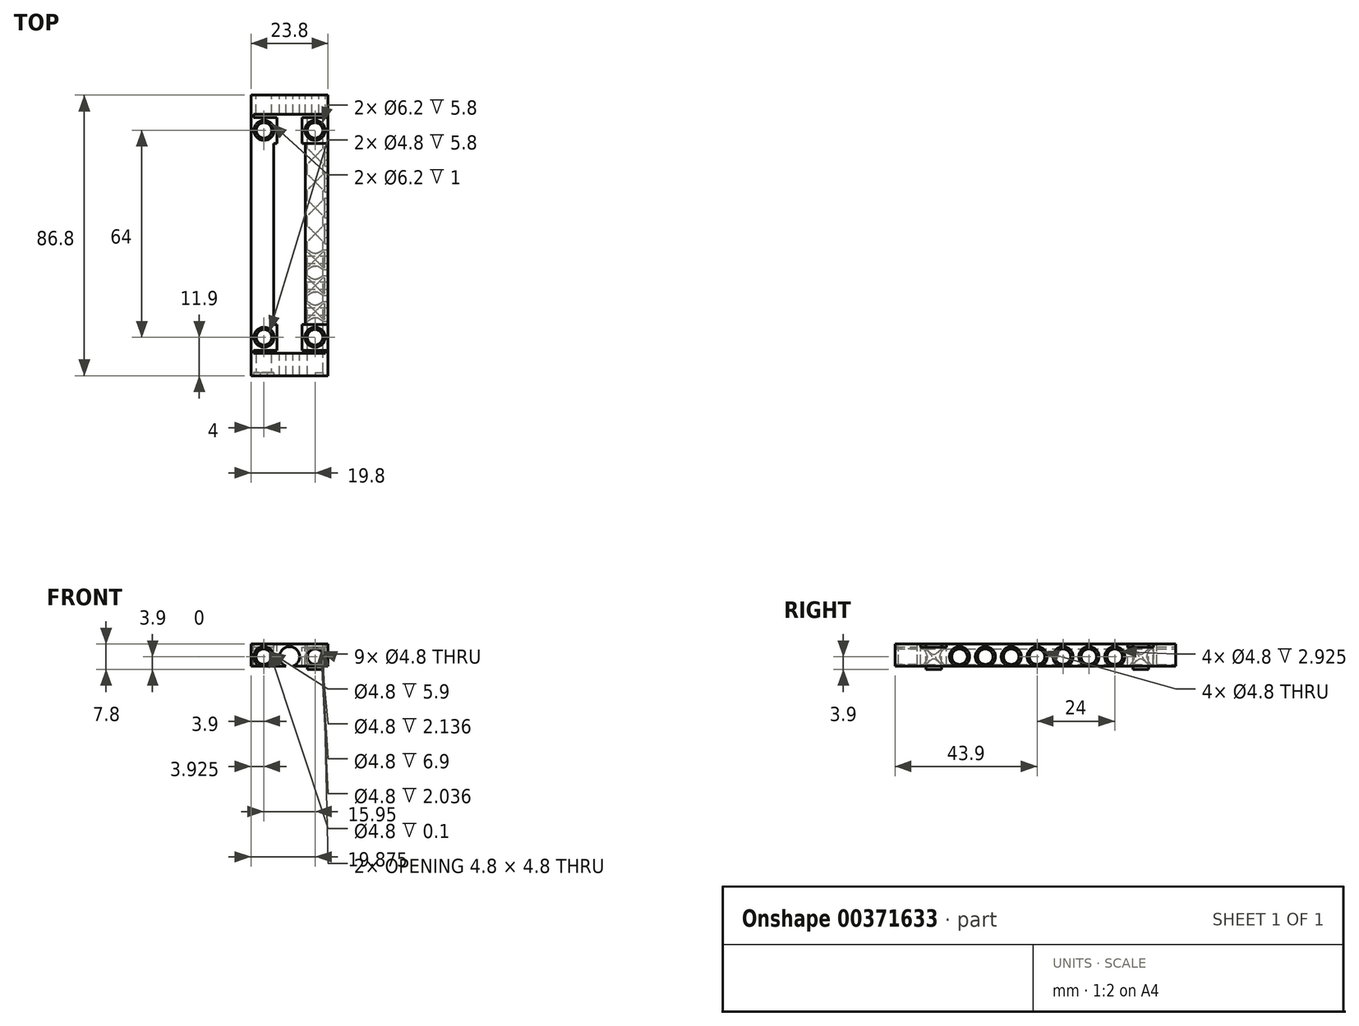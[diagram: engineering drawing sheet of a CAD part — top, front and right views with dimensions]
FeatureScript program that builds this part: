
annotation { "Feature Type Name" : "Feature", "Feature Type Description" : "" }
export const myFeature = defineFeature(function(context is Context, id is Id, definition is map)
    precondition{}
    {
        {
            var Q0;
            Q0=qCreatedBy(makeId("Front.planeOp"),FACE);
            var sketch = newSketch(context, id + "F0", { "sketchPlane" : qUnion([Q0])});
            skLineSegment(sketch, "E0", {"start": v(0, 0) * mm, "end": v(0, 7.8) * mm, "construction": true});
            skLineSegment(sketch, "E1", {"start": v(-19.9, 3.9) * mm, "end": v(0, 3.9) * mm, "construction": true});
            skLineSegment(sketch, "E2", {"start": v(0, 7.8) * mm, "end": v(-4, 7.8) * mm});
            skLineSegment(sketch, "E3", {"start": v(-4, 7.8) * mm, "end": v(-11.9, 7.8) * mm});
            skLineSegment(sketch, "E4", {"start": v(-7.95, 7.8) * mm, "end": v(-8, 0) * mm, "construction": true});
            skCircle(sketch, "E5", {"center": v(0, 3.9) * mm, "radius": 2.4 * mm});
            skCircle(sketch, "E6", {"center": v(0, 3.9) * mm, "radius": 3.1 * mm});
            skCircle(sketch, "E7", {"center": v(-7.98, 3.9) * mm, "radius": 2.4 * mm});
            skCircle(sketch, "E8", {"center": v(-7.98, 3.9) * mm, "radius": 3.1 * mm});
            skLineSegment(sketch, "E9", {"start": v(-11.9, 7.8) * mm, "end": v(-11.9, 0) * mm});
            skLineSegment(sketch, "E10", {"start": v(-11.9, 0) * mm, "end": v(0, 0) * mm});
            skLineSegment(sketch, "E11.MirrorCS", {"start": v(4, 7.8) * mm, "end": v(11.9, 7.8) * mm});
            skLineSegment(sketch, "E12.MirrorCS", {"start": v(0, 7.8) * mm, "end": v(4, 7.8) * mm});
            skCircle(sketch, "E13.MirrorC", {"center": v(7.98, 3.9) * mm, "radius": 3.1 * mm});
            skCircle(sketch, "E14.MirrorC", {"center": v(7.98, 3.9) * mm, "radius": 2.4 * mm});
            skLineSegment(sketch, "E15.MirrorCS", {"start": v(11.9, 7.8) * mm, "end": v(11.9, 0) * mm});
            skLineSegment(sketch, "E16.MirrorCS", {"start": v(11.9, 0) * mm, "end": v(0, 0) * mm});
            skSolve(sketch);
        }
        {
            var Q0;
            Q0=makeQuery(id+"F0.imprint","IMPRINT",FACE,{"disambiguationData":[TD([[makeQuery(id+"F0.imprint","IMPRINT",EDGE,{"derivedFrom":sQuery(id+"F0.wireOp",EDGE,"E2")}),1.0]])]});
            var Q1;
            Q1=makeQuery(id+"F0.imprint","IMPRINT",FACE,{"disambiguationData":[TD([[makeQuery(id+"F0.imprint","IMPRINT",EDGE,{"derivedFrom":sQuery(id+"F0.wireOp",EDGE,"E13.MirrorC")}),-1.0]])]});
            var Q2;
            Q2=makeQuery(id+"F0.imprint","IMPRINT",FACE,{"disambiguationData":[TD([[makeQuery(id+"F0.imprint","IMPRINT",EDGE,{"derivedFrom":sQuery(id+"F0.wireOp",EDGE,"E6")}),-1.0]])]});
            var Q3;
            Q3=makeQuery(id+"F0.imprint","IMPRINT",FACE,{"disambiguationData":[TD([[makeQuery(id+"F0.imprint","IMPRINT",EDGE,{"derivedFrom":sQuery(id+"F0.wireOp",EDGE,"E7")}),-1.0]])]});
            var Q4;
            Q4=makeQuery(id+"F0.imprint","IMPRINT",FACE,{"disambiguationData":[TD([[makeQuery(id+"F0.imprint","IMPRINT",EDGE,{"derivedFrom":sQuery(id+"F0.wireOp",EDGE,"E7")}),1.0]])]});
            var Q5;
            Q5=makeQuery(id+"F0.imprint","IMPRINT",FACE,{"disambiguationData":[TD([[makeQuery(id+"F0.imprint","IMPRINT",EDGE,{"derivedFrom":sQuery(id+"F0.wireOp",EDGE,"E5")}),-1.0]])]});
            var Q6;
            Q6=makeQuery(id+"F0.imprint","IMPRINT",FACE,{"disambiguationData":[TD([[makeQuery(id+"F0.imprint","IMPRINT",EDGE,{"derivedFrom":sQuery(id+"F0.wireOp",EDGE,"E14.MirrorC")}),-1.0]])]});
            extrude(context, id + "F1", {"entities" : qUnion([Q0, Q1, Q2, Q3, Q4, Q5, Q6]), "depth" : 87.8 * mm});
        }
        {
            var Q0;
            Q0=makeQuery(id+"F0.imprint","IMPRINT",FACE,{"disambiguationData":[TD([[makeQuery(id+"F0.imprint","IMPRINT",EDGE,{"derivedFrom":sQuery(id+"F0.wireOp",EDGE,"E13.MirrorC")}),-1.0]])]});
            var Q1;
            Q1=makeQuery(id+"F0.imprint","IMPRINT",FACE,{"disambiguationData":[TD([[makeQuery(id+"F0.imprint","IMPRINT",EDGE,{"derivedFrom":sQuery(id+"F0.wireOp",EDGE,"E6")}),-1.0]])]});
            var Q2;
            Q2=makeQuery(id+"F0.imprint","IMPRINT",FACE,{"disambiguationData":[TD([[makeQuery(id+"F0.imprint","IMPRINT",EDGE,{"derivedFrom":sQuery(id+"F0.wireOp",EDGE,"E7")}),-1.0]])]});
            extrude(context, id + "F2", {"entities" : qUnion([Q0, Q1, Q2]), "operationType" : NewBodyOperationType.REMOVE, "depth" : 1 * mm});
        }
        {
            var Q0;
            Q0=makeQuery(id+"F0.imprint","IMPRINT",FACE,{"disambiguationData":[TD([[makeQuery(id+"F0.imprint","IMPRINT",EDGE,{"derivedFrom":sQuery(id+"F0.wireOp",EDGE,"E7")}),1.0]])]});
            var Q1;
            Q1=makeQuery(id+"F0.imprint","IMPRINT",FACE,{"disambiguationData":[TD([[makeQuery(id+"F0.imprint","IMPRINT",EDGE,{"derivedFrom":sQuery(id+"F0.wireOp",EDGE,"E5")}),-1.0]])]});
            var Q2;
            Q2=makeQuery(id+"F0.imprint","IMPRINT",FACE,{"disambiguationData":[TD([[makeQuery(id+"F0.imprint","IMPRINT",EDGE,{"derivedFrom":sQuery(id+"F0.wireOp",EDGE,"E14.MirrorC")}),-1.0]])]});
            extrude(context, id + "F3", {"entities" : qUnion([Q0, Q1, Q2]), "operationType" : NewBodyOperationType.REMOVE, "depth" : 8 * mm});
        }
        {
            var Q0;
            Q0=makeQuery(id+"F1.opExtrude","SWEPT_FACE",FACE,{"disambiguationData":[OSD([sQuery(id+"F0.wireOp",EDGE,"E2"),sQuery(id+"F0.wireOp",EDGE,"E3"),sQuery(id+"F0.wireOp",EDGE,"E11.MirrorCS"),sQuery(id+"F0.wireOp",EDGE,"E12.MirrorCS")])]});
            var sketch = newSketch(context, id + "F4", { "sketchPlane" : qUnion([Q0])});
            skLineSegment(sketch, "E17", {"start": v(-11.9, 0) * mm, "end": v(-3.9, 0) * mm});
            skLineSegment(sketch, "E18", {"start": v(-3.9, 0) * mm, "end": v(-3.9, -7.9) * mm, "construction": true});
            skLineSegment(sketch, "E19", {"start": v(-3.9, -7.9) * mm, "end": v(-11.9, -7.9) * mm});
            skLineSegment(sketch, "E20", {"start": v(-3.9, -7.9) * mm, "end": v(-3.9, -15.9) * mm});
            skLineSegment(sketch, "E21", {"start": v(-3.9, -15.9) * mm, "end": v(-11.9, -15.9) * mm});
            skLineSegment(sketch, "E22", {"start": v(-3.9, -71.9) * mm, "end": v(-11.9, -71.9) * mm});
            skLineSegment(sketch, "E23", {"start": v(-3.9, -79.9) * mm, "end": v(-11.9, -79.9) * mm});
            skLineSegment(sketch, "E24", {"start": v(-7.9, -71.9) * mm, "end": v(-7.9, -79.9) * mm, "construction": true});
            skLineSegment(sketch, "E25", {"start": v(-3.9, -75.9) * mm, "end": v(-11.9, -75.9) * mm, "construction": true});
            skCircle(sketch, "E26", {"center": v(-7.9, -75.9) * mm, "radius": 2.4 * mm});
            skCircle(sketch, "E27", {"center": v(-7.9, -75.9) * mm, "radius": 3.1 * mm});
            skCircle(sketch, "E28", {"center": v(-7.9, -11.9) * mm, "radius": 2.4 * mm});
            skPoint(sketch, "E28.centerSnap0", {"position": v(-3.9, -11.9) * mm});
            skPoint(sketch, "E28.centerSnap1", {"position": v(-7.9, -15.9) * mm});
            skCircle(sketch, "E29", {"center": v(-7.9, -11.9) * mm, "radius": 3.1 * mm});
            skLineSegment(sketch, "E30", {"start": v(0, 0) * mm, "end": v(0, -43.05) * mm, "construction": true});
            skCircle(sketch, "E31.MirrorC", {"center": v(7.9, -11.9) * mm, "radius": 3.1 * mm});
            skCircle(sketch, "E32.MirrorC", {"center": v(7.9, -11.9) * mm, "radius": 2.4 * mm});
            skLineSegment(sketch, "E33.MirrorCS", {"start": v(3.9, -7.9) * mm, "end": v(11.9, -7.9) * mm});
            skLineSegment(sketch, "E34.MirrorCS", {"start": v(3.9, -15.9) * mm, "end": v(11.9, -15.9) * mm});
            skLineSegment(sketch, "E35.MirrorCS", {"start": v(3.9, -71.9) * mm, "end": v(11.9, -71.9) * mm});
            skLineSegment(sketch, "E36.MirrorCS", {"start": v(3.9, -79.9) * mm, "end": v(11.9, -79.9) * mm});
            skCircle(sketch, "E37.MirrorC", {"center": v(7.9, -75.9) * mm, "radius": 3.1 * mm});
            skCircle(sketch, "E38.MirrorC", {"center": v(7.9, -75.9) * mm, "radius": 2.4 * mm});
            skLineSegment(sketch, "E39", {"start": v(-3.9, -79.9) * mm, "end": v(-3.9, -71.9) * mm});
            skLineSegment(sketch, "E40", {"start": v(-3.9, -71.9) * mm, "end": v(-4.9, -71.9) * mm});
            skLineSegment(sketch, "E41", {"start": v(-4.9, -71.9) * mm, "end": v(-4.9, -15.9) * mm});
            skLineSegment(sketch, "E42", {"start": v(3.9, -7.9) * mm, "end": v(3.9, -15.9) * mm});
            skLineSegment(sketch, "E43.MirrorCS", {"start": v(4.9, -71.9) * mm, "end": v(4.9, -15.9) * mm});
            skLineSegment(sketch, "E44.MirrorCS", {"start": v(3.9, -79.9) * mm, "end": v(3.9, -71.9) * mm});
            skLineSegment(sketch, "E45", {"start": v(11.9, -7.9) * mm, "end": v(11.1, -7.9) * mm});
            skLineSegment(sketch, "E46", {"start": v(11.1, -7.9) * mm, "end": v(11.1, -6.9) * mm});
            skLineSegment(sketch, "E47", {"start": v(-11.9, -7.9) * mm, "end": v(-11.1, -7.9) * mm});
            skLineSegment(sketch, "E48", {"start": v(-11.1, -7.9) * mm, "end": v(-11.1, -6.9) * mm});
            skLineSegment(sketch, "E49", {"start": v(-11.1, -6.9) * mm, "end": v(11.1, -6.9) * mm});
            skLineSegment(sketch, "E50", {"start": v(4.9, -43.9) * mm, "end": v(-4.9, -43.9) * mm, "construction": true});
            skLineSegment(sketch, "E51.MirrorCS", {"start": v(-11.1, -80.9) * mm, "end": v(11.1, -80.9) * mm});
            skLineSegment(sketch, "E52.MirrorCS", {"start": v(11.1, -79.9) * mm, "end": v(11.1, -80.9) * mm});
            skLineSegment(sketch, "E53.MirrorCS", {"start": v(-11.1, -79.9) * mm, "end": v(-11.1, -80.9) * mm});
            skSolve(sketch);
        }
        {
            var Q0;
            Q0=makeQuery(id+"F4.imprint","IMPRINT",FACE,{"disambiguationData":[TD([[makeQuery(id+"F4.imprint","IMPRINT",EDGE,{"derivedFrom":sQuery(id+"F4.wireOp",EDGE,"E28")}),1.0]])]});
            var Q1;
            Q1=makeQuery(id+"F4.imprint","IMPRINT",FACE,{"disambiguationData":[TD([[makeQuery(id+"F4.imprint","IMPRINT",EDGE,{"derivedFrom":sQuery(id+"F4.wireOp",EDGE,"E26")}),1.0]])]});
            var Q2;
            Q2=makeQuery(id+"F4.imprint","IMPRINT",FACE,{"disambiguationData":[TD([[makeQuery(id+"F4.imprint","IMPRINT",EDGE,{"derivedFrom":sQuery(id+"F4.wireOp",EDGE,"E38.MirrorC")}),-1.0]])]});
            var Q3;
            Q3=makeQuery(id+"F4.imprint","IMPRINT",FACE,{"disambiguationData":[TD([[makeQuery(id+"F4.imprint","IMPRINT",EDGE,{"derivedFrom":sQuery(id+"F4.wireOp",EDGE,"E32.MirrorC")}),-1.0]])]});
            extrude(context, id + "F5", {"entities" : qUnion([Q0, Q1, Q2, Q3]), "operationType" : NewBodyOperationType.REMOVE, "oppositeDirection" : true, "depth" : 25 * mm});
        }
        {
            var Q0;
            Q0=makeQuery(id+"F4.imprint","IMPRINT",FACE,{"disambiguationData":[TD([[makeQuery(id+"F4.imprint","IMPRINT",EDGE,{"derivedFrom":sQuery(id+"F4.wireOp",EDGE,"E28")}),-1.0]])]});
            var Q1;
            Q1=makeQuery(id+"F4.imprint","IMPRINT",FACE,{"disambiguationData":[TD([[makeQuery(id+"F4.imprint","IMPRINT",EDGE,{"derivedFrom":sQuery(id+"F4.wireOp",EDGE,"E31.MirrorC")}),-1.0]])]});
            var Q2;
            Q2=makeQuery(id+"F4.imprint","IMPRINT",FACE,{"disambiguationData":[TD([[makeQuery(id+"F4.imprint","IMPRINT",EDGE,{"derivedFrom":sQuery(id+"F4.wireOp",EDGE,"E26")}),-1.0]])]});
            var Q3;
            Q3=makeQuery(id+"F4.imprint","IMPRINT",FACE,{"disambiguationData":[TD([[makeQuery(id+"F4.imprint","IMPRINT",EDGE,{"derivedFrom":sQuery(id+"F4.wireOp",EDGE,"E37.MirrorC")}),-1.0]])]});
            extrude(context, id + "F6", {"entities" : qUnion([Q0, Q1, Q2, Q3]), "operationType" : NewBodyOperationType.REMOVE, "oppositeDirection" : true, "depth" : 1 * mm});
        }
        {
            var Q0;
            Q0=makeQuery(id+"F1.opExtrude","SWEPT_FACE",FACE,{"disambiguationData":[OSD([sQuery(id+"F0.wireOp",EDGE,"E10"),sQuery(id+"F0.wireOp",EDGE,"E16.MirrorCS")])]});
            var sketch = newSketch(context, id + "F7", { "sketchPlane" : qUnion([Q0])});
            skCircle(sketch, "E54", {"center": v(-7.9, 75.9) * mm, "radius": 3.1 * mm});
            skCircle(sketch, "E55", {"center": v(-7.9, 11.9) * mm, "radius": 3.1 * mm});
            skCircle(sketch, "E56", {"center": v(7.9, 11.9) * mm, "radius": 3.1 * mm});
            skCircle(sketch, "E57", {"center": v(7.9, 75.9) * mm, "radius": 3.1 * mm});
            skSolve(sketch);
        }
        {
            var Q0;
            Q0=makeQuery(id+"F7.imprint","IMPRINT",FACE,{"disambiguationData":[TD([[makeQuery(id+"F7.imprint","IMPRINT",EDGE,{"derivedFrom":sQuery(id+"F7.wireOp",EDGE,"E57")}),1.0]])]});
            var Q1;
            Q1=makeQuery(id+"F7.imprint","IMPRINT",FACE,{"disambiguationData":[TD([[makeQuery(id+"F7.imprint","IMPRINT",EDGE,{"derivedFrom":sQuery(id+"F7.wireOp",EDGE,"E54")}),1.0]])]});
            var Q2;
            Q2=makeQuery(id+"F7.imprint","IMPRINT",FACE,{"disambiguationData":[TD([[makeQuery(id+"F7.imprint","IMPRINT",EDGE,{"derivedFrom":sQuery(id+"F7.wireOp",EDGE,"E55")}),1.0]])]});
            var Q3;
            Q3=makeQuery(id+"F7.imprint","IMPRINT",FACE,{"disambiguationData":[TD([[makeQuery(id+"F7.imprint","IMPRINT",EDGE,{"derivedFrom":sQuery(id+"F7.wireOp",EDGE,"E56")}),1.0]])]});
            extrude(context, id + "F8", {"entities" : qUnion([Q0, Q1, Q2, Q3]), "operationType" : NewBodyOperationType.REMOVE, "oppositeDirection" : true, "depth" : 1 * mm});
        }
        {
            var Q0;
            Q0=makeQuery(id+"F1.opExtrude","SWEPT_FACE",FACE,{"disambiguationData":[OSD([sQuery(id+"F0.wireOp",EDGE,"E15.MirrorCS")])]});
            var sketch = newSketch(context, id + "F9", { "sketchPlane" : qUnion([Q0])});
            skLineSegment(sketch, "E58", {"start": v(0, 7.8) * mm, "end": v(-15.9, 7.8) * mm});
            skLineSegment(sketch, "E59", {"start": v(-15.9, 7.8) * mm, "end": v(-15.9, 0) * mm});
            skLineSegment(sketch, "E60", {"start": v(-15.9, 3.9) * mm, "end": v(-71.9, 3.9) * mm, "construction": true});
            skLineSegment(sketch, "E61", {"start": v(-15.9, 7.8) * mm, "end": v(-23.9, 7.8) * mm, "construction": true});
            skLineSegment(sketch, "E62", {"start": v(-23.9, 7.8) * mm, "end": v(-31.9, 7.8) * mm, "construction": true});
            skLineSegment(sketch, "E63", {"start": v(-31.9, 7.8) * mm, "end": v(-39.9, 7.8) * mm, "construction": true});
            skLineSegment(sketch, "E64", {"start": v(-39.9, 7.8) * mm, "end": v(-47.9, 7.8) * mm, "construction": true});
            skLineSegment(sketch, "E65", {"start": v(-47.9, 7.8) * mm, "end": v(-55.9, 7.8) * mm, "construction": true});
            skLineSegment(sketch, "E66", {"start": v(-55.9, 7.8) * mm, "end": v(-63.9, 7.8) * mm, "construction": true});
            skLineSegment(sketch, "E67", {"start": v(-63.9, 7.8) * mm, "end": v(-71.9, 7.8) * mm, "construction": true});
            skLineSegment(sketch, "E68", {"start": v(-71.9, 7.8) * mm, "end": v(-71.9, 0) * mm});
            skLineSegment(sketch, "E69", {"start": v(-19.9, 7.8) * mm, "end": v(-19.9, 0) * mm, "construction": true});
            skLineSegment(sketch, "E70", {"start": v(-27.9, 7.8) * mm, "end": v(-27.9, 0) * mm, "construction": true});
            skLineSegment(sketch, "E71", {"start": v(-35.9, 7.8) * mm, "end": v(-35.9, 0) * mm, "construction": true});
            skLineSegment(sketch, "E72", {"start": v(-43.9, 7.8) * mm, "end": v(-43.9, 0) * mm, "construction": true});
            skCircle(sketch, "E73", {"center": v(-19.9, 3.9) * mm, "radius": 2.4 * mm});
            skCircle(sketch, "E74", {"center": v(-19.9, 3.9) * mm, "radius": 3.1 * mm});
            skCircle(sketch, "E75", {"center": v(-27.9, 3.9) * mm, "radius": 2.4 * mm});
            skCircle(sketch, "E76", {"center": v(-27.9, 3.9) * mm, "radius": 3.1 * mm});
            skCircle(sketch, "E77", {"center": v(-35.9, 3.9) * mm, "radius": 2.4 * mm});
            skCircle(sketch, "E78", {"center": v(-35.9, 3.9) * mm, "radius": 3.1 * mm});
            skCircle(sketch, "E79", {"center": v(-43.9, 3.9) * mm, "radius": 2.4 * mm});
            skCircle(sketch, "E80", {"center": v(-43.9, 3.9) * mm, "radius": 3.1 * mm});
            skCircle(sketch, "E81.MirrorC", {"center": v(-51.9, 3.9) * mm, "radius": 2.4 * mm});
            skCircle(sketch, "E82.MirrorC", {"center": v(-51.9, 3.9) * mm, "radius": 3.1 * mm});
            skCircle(sketch, "E83.MirrorC", {"center": v(-59.9, 3.9) * mm, "radius": 2.4 * mm});
            skCircle(sketch, "E84.MirrorC", {"center": v(-59.9, 3.9) * mm, "radius": 3.1 * mm});
            skCircle(sketch, "E85.MirrorC", {"center": v(-67.9, 3.9) * mm, "radius": 2.4 * mm});
            skCircle(sketch, "E86.MirrorC", {"center": v(-67.9, 3.9) * mm, "radius": 3.1 * mm});
            skSolve(sketch);
        }
        {
            var Q0;
            Q0=makeQuery(id+"F9.imprint","IMPRINT",FACE,{"disambiguationData":[TD([[makeQuery(id+"F9.imprint","IMPRINT",EDGE,{"derivedFrom":sQuery(id+"F9.wireOp",EDGE,"E85.MirrorC")}),-1.0]])]});
            var Q1;
            Q1=makeQuery(id+"F9.imprint","IMPRINT",FACE,{"disambiguationData":[TD([[makeQuery(id+"F9.imprint","IMPRINT",EDGE,{"derivedFrom":sQuery(id+"F9.wireOp",EDGE,"E83.MirrorC")}),-1.0]])]});
            var Q2;
            Q2=makeQuery(id+"F9.imprint","IMPRINT",FACE,{"disambiguationData":[TD([[makeQuery(id+"F9.imprint","IMPRINT",EDGE,{"derivedFrom":sQuery(id+"F9.wireOp",EDGE,"E81.MirrorC")}),-1.0]])]});
            var Q3;
            Q3=makeQuery(id+"F9.imprint","IMPRINT",FACE,{"disambiguationData":[TD([[makeQuery(id+"F9.imprint","IMPRINT",EDGE,{"derivedFrom":sQuery(id+"F9.wireOp",EDGE,"E79")}),1.0]])]});
            var Q4;
            Q4=makeQuery(id+"F9.imprint","IMPRINT",FACE,{"disambiguationData":[TD([[makeQuery(id+"F9.imprint","IMPRINT",EDGE,{"derivedFrom":sQuery(id+"F9.wireOp",EDGE,"E77")}),1.0]])]});
            var Q5;
            Q5=makeQuery(id+"F9.imprint","IMPRINT",FACE,{"disambiguationData":[TD([[makeQuery(id+"F9.imprint","IMPRINT",EDGE,{"derivedFrom":sQuery(id+"F9.wireOp",EDGE,"E75")}),1.0]])]});
            var Q6;
            Q6=makeQuery(id+"F9.imprint","IMPRINT",FACE,{"disambiguationData":[TD([[makeQuery(id+"F9.imprint","IMPRINT",EDGE,{"derivedFrom":sQuery(id+"F9.wireOp",EDGE,"E73")}),1.0]])]});
            extrude(context, id + "F10", {"entities" : qUnion([Q0, Q1, Q2, Q3, Q4, Q5, Q6]), "operationType" : NewBodyOperationType.REMOVE, "oppositeDirection" : true, "depth" : 8 * mm});
        }
        {
            var Q0;
            Q0=makeQuery(id+"F9.imprint","IMPRINT",FACE,{"disambiguationData":[TD([[makeQuery(id+"F9.imprint","IMPRINT",EDGE,{"derivedFrom":sQuery(id+"F9.wireOp",EDGE,"E85.MirrorC")}),1.0]])]});
            var Q1;
            Q1=makeQuery(id+"F9.imprint","IMPRINT",FACE,{"disambiguationData":[TD([[makeQuery(id+"F9.imprint","IMPRINT",EDGE,{"derivedFrom":sQuery(id+"F9.wireOp",EDGE,"E83.MirrorC")}),1.0]])]});
            var Q2;
            Q2=makeQuery(id+"F9.imprint","IMPRINT",FACE,{"disambiguationData":[TD([[makeQuery(id+"F9.imprint","IMPRINT",EDGE,{"derivedFrom":sQuery(id+"F9.wireOp",EDGE,"E81.MirrorC")}),1.0]])]});
            var Q3;
            Q3=makeQuery(id+"F9.imprint","IMPRINT",FACE,{"disambiguationData":[TD([[makeQuery(id+"F9.imprint","IMPRINT",EDGE,{"derivedFrom":sQuery(id+"F9.wireOp",EDGE,"E79")}),-1.0]])]});
            var Q4;
            Q4=makeQuery(id+"F9.imprint","IMPRINT",FACE,{"disambiguationData":[TD([[makeQuery(id+"F9.imprint","IMPRINT",EDGE,{"derivedFrom":sQuery(id+"F9.wireOp",EDGE,"E77")}),-1.0]])]});
            var Q5;
            Q5=makeQuery(id+"F9.imprint","IMPRINT",FACE,{"disambiguationData":[TD([[makeQuery(id+"F9.imprint","IMPRINT",EDGE,{"derivedFrom":sQuery(id+"F9.wireOp",EDGE,"E75")}),-1.0]])]});
            var Q6;
            Q6=makeQuery(id+"F9.imprint","IMPRINT",FACE,{"disambiguationData":[TD([[makeQuery(id+"F9.imprint","IMPRINT",EDGE,{"derivedFrom":sQuery(id+"F9.wireOp",EDGE,"E73")}),-1.0]])]});
            extrude(context, id + "F11", {"entities" : qUnion([Q0, Q1, Q2, Q3, Q4, Q5, Q6]), "operationType" : NewBodyOperationType.REMOVE, "oppositeDirection" : true, "depth" : 1 * mm});
        }
        {
            var Q0;
            Q0=makeQuery(id+"F4.imprint","IMPRINT",FACE,{"disambiguationData":[TD([[makeQuery(id+"F4.imprint","IMPRINT",EDGE,{"derivedFrom":sQuery(id+"F4.wireOp",EDGE,"E20")}),1.0]])]});
            extrude(context, id + "F12", {"entities" : qUnion([Q0]), "operationType" : NewBodyOperationType.REMOVE, "oppositeDirection" : true, "depth" : 7 * mm});
        }
        {
            var Q0;
            Q0=makeQuery(id+"F1.opExtrude","CAP_FACE",FACE,{"disambiguationData":[OSD([sQuery(id+"F0.wireOp",EDGE,"E2"),sQuery(id+"F0.wireOp",EDGE,"E3"),sQuery(id+"F0.wireOp",EDGE,"E9"),sQuery(id+"F0.wireOp",EDGE,"E10"),sQuery(id+"F0.wireOp",EDGE,"E11.MirrorCS"),sQuery(id+"F0.wireOp",EDGE,"E12.MirrorCS"),sQuery(id+"F0.wireOp",EDGE,"E15.MirrorCS"),sQuery(id+"F0.wireOp",EDGE,"E16.MirrorCS")])],"isStart":false});
            var sketch = newSketch(context, id + "F13", { "sketchPlane" : qUnion([Q0])});
            skLineSegment(sketch, "E87", {"start": v(0, 0) * mm, "end": v(0, 7.8) * mm, "construction": true});
            skLineSegment(sketch, "E88", {"start": v(0, 3.9) * mm, "end": v(-11.9, 3.9) * mm, "construction": true});
            skLineSegment(sketch, "E89", {"start": v(0, 7.8) * mm, "end": v(-4, 7.8) * mm, "construction": true});
            skLineSegment(sketch, "E90", {"start": v(-4, 7.8) * mm, "end": v(-8, 7.8) * mm, "construction": true});
            skLineSegment(sketch, "E91", {"start": v(-8, 7.8) * mm, "end": v(-8, 0) * mm, "construction": true});
            skCircle(sketch, "E92", {"center": v(-8, 3.9) * mm, "radius": 2.4 * mm});
            skCircle(sketch, "E93", {"center": v(-8, 3.9) * mm, "radius": 3.1 * mm});
            skCircle(sketch, "E94", {"center": v(0, 3.9) * mm, "radius": 2.4 * mm});
            skCircle(sketch, "E95", {"center": v(0, 3.9) * mm, "radius": 3.1 * mm});
            skCircle(sketch, "E96.MirrorC", {"center": v(8, 3.9) * mm, "radius": 2.4 * mm});
            skCircle(sketch, "E97.MirrorC", {"center": v(8, 3.9) * mm, "radius": 3.1 * mm});
            skSolve(sketch);
        }
        {
            var Q0;
            Q0=makeQuery(id+"F13.imprint","IMPRINT",FACE,{"disambiguationData":[TD([[makeQuery(id+"F13.imprint","IMPRINT",EDGE,{"derivedFrom":sQuery(id+"F13.wireOp",EDGE,"E92")}),1.0]])]});
            var Q1;
            Q1=makeQuery(id+"F13.imprint","IMPRINT",FACE,{"disambiguationData":[TD([[makeQuery(id+"F13.imprint","IMPRINT",EDGE,{"derivedFrom":sQuery(id+"F13.wireOp",EDGE,"E94")}),1.0]])]});
            var Q2;
            Q2=makeQuery(id+"F13.imprint","IMPRINT",FACE,{"disambiguationData":[TD([[makeQuery(id+"F13.imprint","IMPRINT",EDGE,{"derivedFrom":sQuery(id+"F13.wireOp",EDGE,"E96.MirrorC")}),-1.0]])]});
            extrude(context, id + "F14", {"entities" : qUnion([Q0, Q1, Q2]), "operationType" : NewBodyOperationType.REMOVE, "oppositeDirection" : true, "depth" : 7.9 * mm});
        }
        {
            var Q0;
            Q0=makeQuery(id+"F13.imprint","IMPRINT",FACE,{"disambiguationData":[TD([[makeQuery(id+"F13.imprint","IMPRINT",EDGE,{"derivedFrom":sQuery(id+"F13.wireOp",EDGE,"E92")}),-1.0]])]});
            var Q1;
            Q1=makeQuery(id+"F13.imprint","IMPRINT",FACE,{"disambiguationData":[TD([[makeQuery(id+"F13.imprint","IMPRINT",EDGE,{"derivedFrom":sQuery(id+"F13.wireOp",EDGE,"E94")}),-1.0]])]});
            var Q2;
            Q2=makeQuery(id+"F13.imprint","IMPRINT",FACE,{"disambiguationData":[TD([[makeQuery(id+"F13.imprint","IMPRINT",EDGE,{"derivedFrom":sQuery(id+"F13.wireOp",EDGE,"E96.MirrorC")}),1.0]])]});
            extrude(context, id + "F15", {"entities" : qUnion([Q0, Q1, Q2]), "operationType" : NewBodyOperationType.REMOVE, "oppositeDirection" : true, "depth" : 1 * mm});
        }
    });
